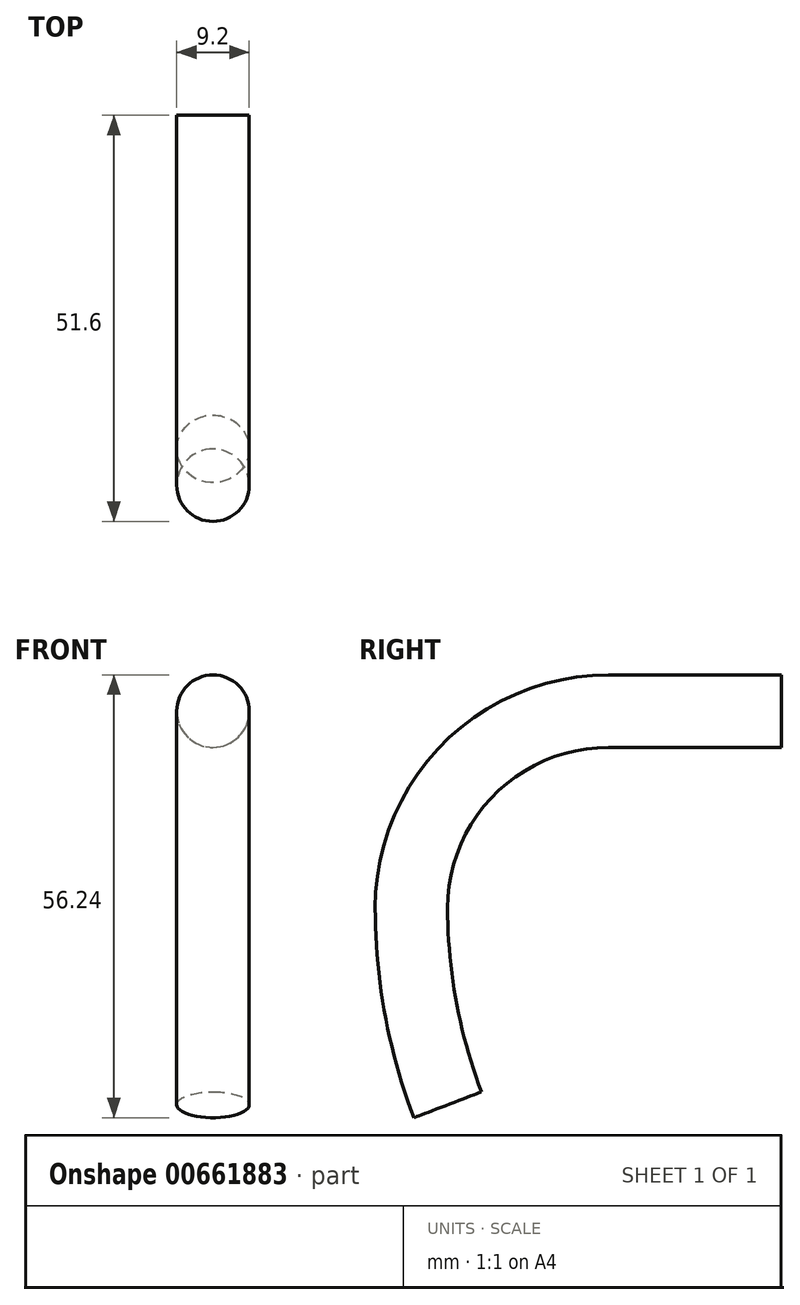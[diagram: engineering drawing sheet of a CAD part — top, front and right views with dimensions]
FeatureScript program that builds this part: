
annotation { "Feature Type Name" : "Feature", "Feature Type Description" : "" }
export const myFeature = defineFeature(function(context is Context, id is Id, definition is map)
    precondition{}
    {
        {
            var Q0;
            Q0=qCreatedBy(makeId("Front.planeOp"),FACE);
            var sketch = newSketch(context, id + "F0", { "sketchPlane" : qUnion([Q0])});
            skCircle(sketch, "E0", {"center": v(0, 0) * mm, "radius": 4.6 * mm});
            skSolve(sketch);
        }
        {
            var Q0;
            Q0=qCreatedBy(makeId("Right.planeOp"),FACE);
            var sketch = newSketch(context, id + "F1", { "sketchPlane" : qUnion([Q0])});
            skLineSegment(sketch, "E1", {"start": v(0, 0) * mm, "end": v(-22, 0) * mm});
            skArc(sketch, "E2", {"start": v(-22, 0) * mm, "mid": v(-39.68, -7.32) * mm, "end": v(-47, -25) * mm});
            skArc(sketch, "E3", {"start": v(-47, -25) * mm, "mid": v(-45.84, -37.71) * mm, "end": v(-42.38, -50) * mm});
            skSolve(sketch);
        }
        {
            var Q0;
            Q0=makeQuery(id+"F0.imprint","IMPRINT",FACE,{"disambiguationData":[TD([[makeQuery(id+"F0.imprint","IMPRINT",EDGE,{"derivedFrom":sQuery(id+"F0.wireOp",EDGE,"E0")}),1.0]])]});
            var Q1;
            Q1=sQuery(id+"F1.wireOp",EDGE,"E1");
            var Q2;
            Q2=sQuery(id+"F1.wireOp",EDGE,"E2");
            var Q3;
            Q3=sQuery(id+"F1.wireOp",EDGE,"E3");
            sweep(context, id + "F2", {"profiles" : qUnion([Q0]), "path" : qUnion([Q1, Q2, Q3])});
        }
    });
